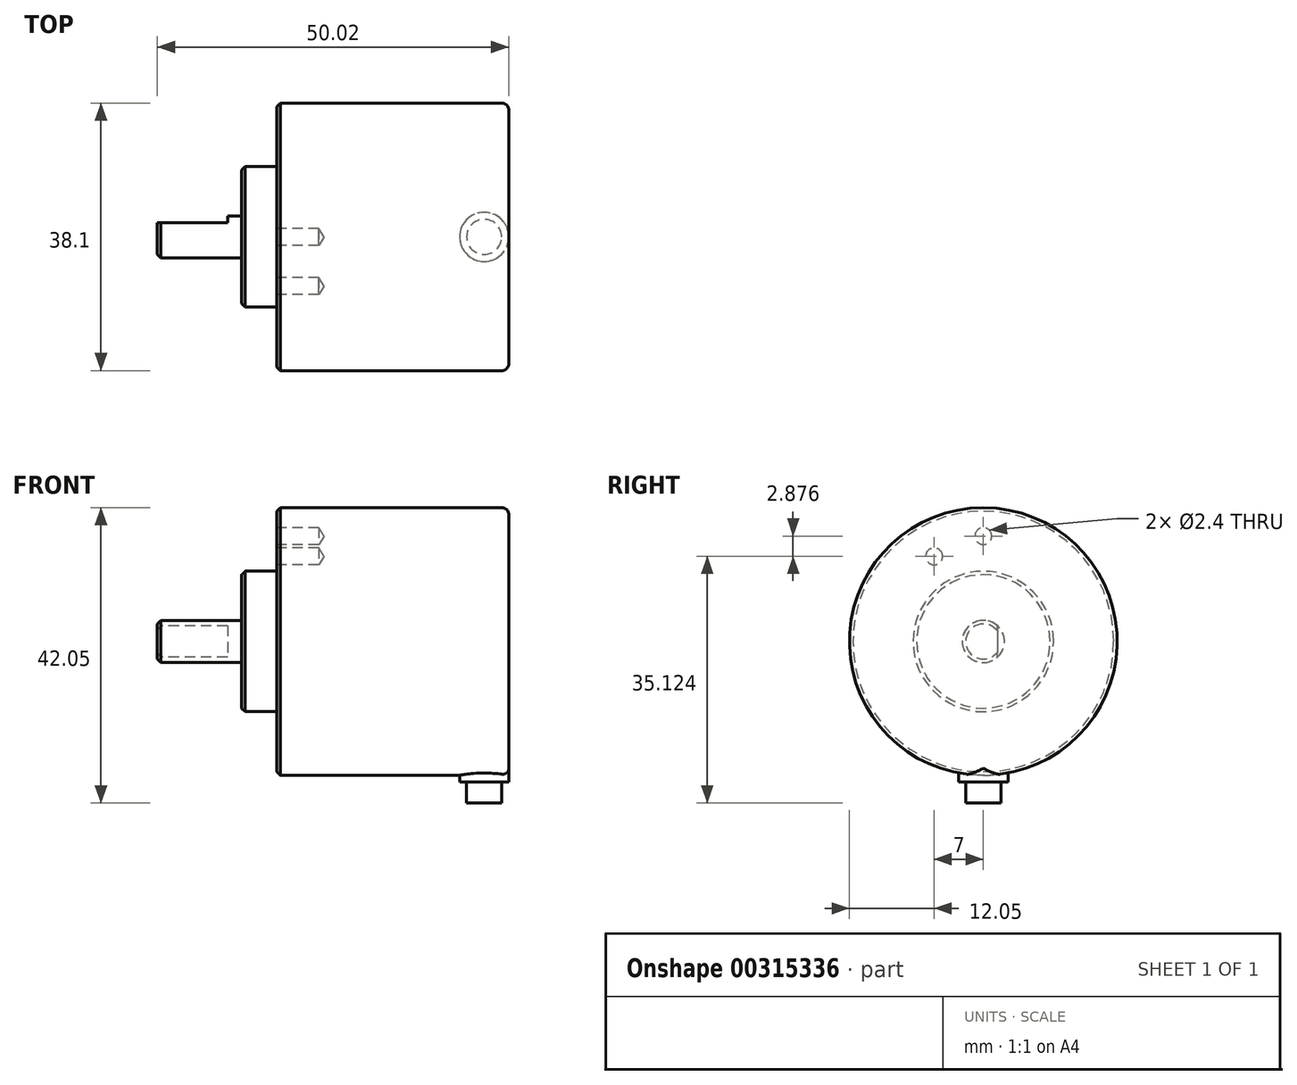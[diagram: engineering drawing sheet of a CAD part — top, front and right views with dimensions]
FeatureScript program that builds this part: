
annotation { "Feature Type Name" : "Feature", "Feature Type Description" : "" }
export const myFeature = defineFeature(function(context is Context, id is Id, definition is map)
    precondition{}
    {
        {
            var Q0;
            Q0=qCreatedBy(makeId("Right.planeOp"),FACE);
            var sketch = newSketch(context, id + "F0", { "sketchPlane" : qUnion([Q0])});
            skCircle(sketch, "E0", {"center": v(0, 0) * mm, "radius": 19.05 * mm});
            skSolve(sketch);
        }
        {
            var Q0;
            Q0 = qSketchRegion(id + "F0", true);
            extrude(context, id + "F1", {"entities" : qUnion([Q0]), "depth" : 33.02 * mm});
        }
        {
            var Q0;
            Q0=makeQuery(id+"F1.opExtrude","CAP_FACE",FACE,{"disambiguationData":[OSD([sQuery(id+"F0.wireOp",EDGE,"E0")])],"isStart":true});
            var sketch = newSketch(context, id + "F2", { "sketchPlane" : qUnion([Q0])});
            skCircle(sketch, "E1", {"center": v(0, 0) * mm, "radius": 10 * mm});
            skLineSegment(sketch, "E2", {"start": v(0, 0) * mm, "end": v(0, 15) * mm, "construction": true});
            skLineSegment(sketch, "E3", {"start": v(0, 0) * mm, "end": v(7, 12.12) * mm, "construction": true});
            skSolve(sketch);
        }
        {
            var Q0;
            Q0 = qSketchRegion(id + "F2", true);
            extrude(context, id + "F3", {"entities" : qUnion([Q0]), "operationType" : NewBodyOperationType.ADD, "depth" : 5 * mm});
        }
        {
            var Q0;
            Q0=sQuery(id+"F2.wireOp",VERTEX,"E2.end");
            var Q1;
            Q1=sQuery(id+"F2.wireOp",VERTEX,"E3.end");
            var Q2;
            Q2=makeQuery(id+"F1.opExtrude","SWEPT_BODY",BODY,{"disambiguationData":[OSD([sQuery(id+"F0.wireOp",EDGE,"E0")])]});
            hole(context, id + "F4", {"style" : HoleStyle.SIMPLE, "endStyle" : HoleEndStyle.BLIND, "standardTappedOrClearance" : lookupTablePath({ "standard" : "ISO", "engagement" : "75%", "pitch" : "0.6 mm", "size" : "M3", "type" : "Tapped" }), "standardBlindInLast" : lookupTablePath({ "standard" : "ISO", "engagement" : "75%", "pitch" : "0.6 mm", "size" : "M3", "type" : "Tapped" }), "holeDiameter" : 2.4 * mm, "showTappedDepth" : true, "holeDepth" : 6 * mm, "tappedDepth" : 4.2 * mm, "tapClearance" : 3, "locations" : qUnion([Q0, Q1]), "scope" : qUnion([Q2])});
        }
        {
            var Q0;
            Q0=makeQuery(id+"F1.opExtrude","CAP_EDGE",EDGE,{"disambiguationData":[OSD([sQuery(id+"F0.wireOp",EDGE,"E0")])],"isStart":true});
            var Q1;
            Q1=makeQuery(id+"F3.opExtrude","CAP_EDGE",EDGE,{"disambiguationData":[OSD([sQuery(id+"F2.wireOp",EDGE,"E1")])],"isStart":false});
            chamfer(context, id + "F5", {"entities" : qUnion([Q0, Q1]), "width" : 0.5 * mm, "tangentPropagation" : true});
        }
        {
            var Q0;
            Q0=makeQuery(id+"F1.opExtrude","CAP_EDGE",EDGE,{"disambiguationData":[OSD([sQuery(id+"F0.wireOp",EDGE,"E0")])],"isStart":false});
            fillet(context, id + "F6", {"entities" : qUnion([Q0]), "radius" : 1 * mm, "tangentPropagation" : true, "allowEdgeOverflow" : false});
        }
        {
            var Q0;
            Q0=makeQuery(id+"F3.opExtrude","CAP_FACE",FACE,{"disambiguationData":[OSD([sQuery(id+"F2.wireOp",EDGE,"E1")])],"isStart":false});
            var sketch = newSketch(context, id + "F7", { "sketchPlane" : qUnion([Q0])});
            skCircle(sketch, "E4", {"center": v(0, 0) * mm, "radius": 3 * mm});
            skSolve(sketch);
        }
        {
            var Q0;
            Q0 = qSketchRegion(id + "F7", true);
            extrude(context, id + "F8", {"entities" : qUnion([Q0]), "depth" : 12 * mm});
        }
        {
            var Q0;
            Q0=makeQuery(id+"F8.opExtrude","CAP_FACE",FACE,{"disambiguationData":[OSD([sQuery(id+"F7.wireOp",EDGE,"E4")])],"isStart":false});
            var sketch = newSketch(context, id + "F9", { "sketchPlane" : qUnion([Q0])});
            skArc(sketch, "E5", {"start": v(-2, -2.24) * mm, "mid": v(-3, 0) * mm, "end": v(-2, 2.24) * mm});
            skLineSegment(sketch, "E6", {"start": v(-2, 2.24) * mm, "end": v(-2, -2.24) * mm});
            skSolve(sketch);
        }
        {
            var Q0;
            Q0 = qSketchRegion(id + "F9", true);
            extrude(context, id + "F10", {"entities" : qUnion([Q0]), "operationType" : NewBodyOperationType.REMOVE, "oppositeDirection" : true, "depth" : 10 * mm});
        }
        {
            var Q0;
            Q0=makeQuery(id+"F8.opExtrude","CAP_EDGE",EDGE,{"disambiguationData":[OSD([sQuery(id+"F7.wireOp",EDGE,"E4")])],"isStart":false});
            chamfer(context, id + "F11", {"entities" : qUnion([Q0]), "width" : 0.5 * mm, "tangentPropagation" : true});
        }
        {
            var Q0;
            Q0=qCreatedBy(makeId("Top.planeOp"),FACE);
            var sketch = newSketch(context, id + "F12", { "sketchPlane" : qUnion([Q0])});
            skCircle(sketch, "E7", {"center": v(29.52, 0) * mm, "radius": 3.5 * mm});
            skSolve(sketch);
        }
        {
            var Q0;
            Q0 = qSketchRegion(id + "F12", true);
            extrude(context, id + "F13", {"entities" : qUnion([Q0]), "operationType" : NewBodyOperationType.ADD, "oppositeDirection" : true, "depth" : 20 * mm});
        }
        {
            var Q0;
            Q0=makeQuery(id+"F13.opExtrude","CAP_FACE",FACE,{"disambiguationData":[OSD([sQuery(id+"F12.wireOp",EDGE,"E7")])],"isStart":false});
            var sketch = newSketch(context, id + "F14", { "sketchPlane" : qUnion([Q0])});
            skCircle(sketch, "E8", {"center": v(29.52, 0) * mm, "radius": 2.5 * mm});
            skSolve(sketch);
        }
        {
            var Q0;
            Q0 = qSketchRegion(id + "F14", true);
            extrude(context, id + "F15", {"entities" : qUnion([Q0]), "operationType" : NewBodyOperationType.ADD, "depth" : 3 * mm});
        }
    });
